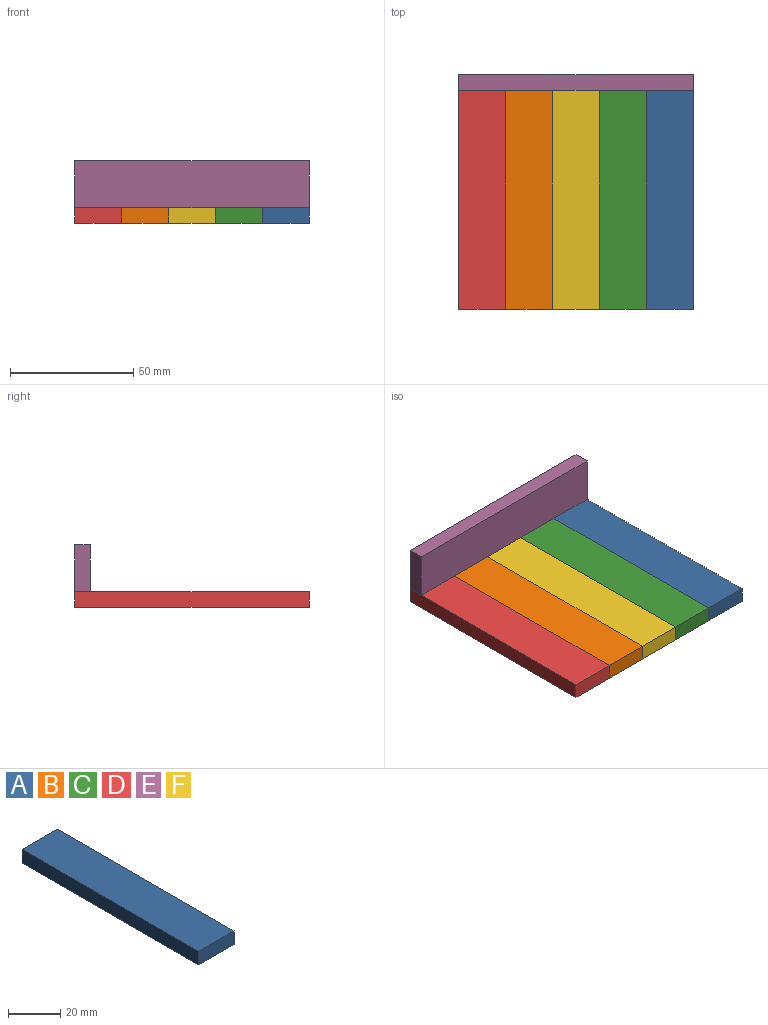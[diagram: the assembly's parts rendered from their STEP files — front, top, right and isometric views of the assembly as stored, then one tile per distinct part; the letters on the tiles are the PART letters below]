
ASSEMBLY  parts=6 mates=5
PART A: 6 faces, bbox 19.1x95.3x6.4 mm
  f0: plane 95.25x19.05mm, normal (0,0,-1), area 1814.5mm2, adj f1,f3,f4,f5
  f1: plane 95.25x6.35mm, normal (1,0,0), area 604.8mm2, adj f0,f2,f4,f5
  f2: plane 95.25x19.05mm, normal (0,0,1), area 1814.5mm2, adj f1,f3,f4,f5
  f3: plane 95.25x6.35mm, normal (-1,0,0), area 604.8mm2, adj f0,f2,f4,f5
  f4: plane 19.05x6.35mm, normal (0,-1,0), area 121mm2, adj f0,f1,f2,f3
  f5: plane 19.05x6.35mm, normal (0,1,0), area 121mm2, adj f0,f1,f2,f3
PART B: same geometry as A
PART C: same geometry as A
PART D: same geometry as A
PART E: same geometry as A
PART F: same geometry as A
PLACE A t=(0,0,-3.17)mm
PLACE B t=(-57.15,0,-3.17)mm
PLACE C t=(-19.05,0,-3.17)mm
PLACE D t=(-76.2,0,-3.17)mm
PLACE E rot(axis=(0.58,-0.58,0.58),120deg) t=(-38.1,44.45,9.52)mm
PLACE F t=(-38.1,0,-3.17)mm
MATE fastened B.f1 <-> F.f3  axis (1,0,0) through (-47.62,0,-3.17)mm
MATE fastened C.f1 <-> A.f3  axis (1,0,0) through (-9.52,-47.63,-3.17)mm
MATE fastened D.f1 <-> B.f3  axis (1,0,0) through (-66.68,0,-3.17)mm
MATE fastened F.f1 <-> C.f3  axis (1,0,0) through (-28.58,0,-3.17)mm
MATE fastened E.f3 <-> F.f2  axis (0,0,-1) through (-38.1,47.63,0)mm
